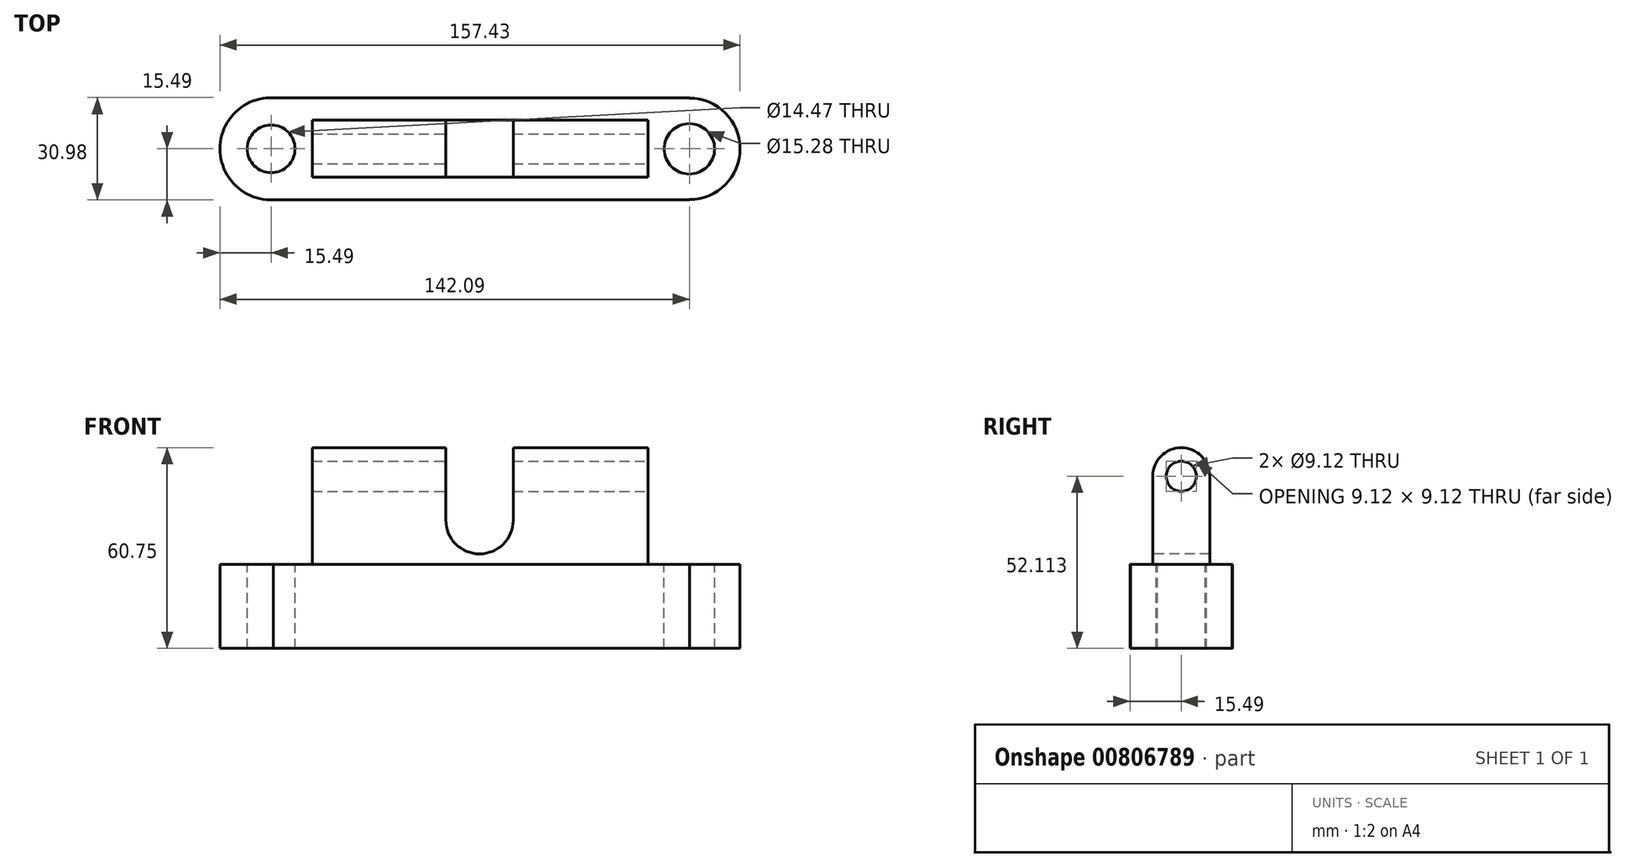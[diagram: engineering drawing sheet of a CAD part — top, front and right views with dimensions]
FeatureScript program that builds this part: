
annotation { "Feature Type Name" : "Feature", "Feature Type Description" : "" }
export const myFeature = defineFeature(function(context is Context, id is Id, definition is map)
    precondition{}
    {
        {
            var Q0;
            Q0=qCreatedBy(makeId("Top.planeOp"),FACE);
            var sketch = newSketch(context, id + "F0", { "sketchPlane" : qUnion([Q0])});
            skLineSegment(sketch, "E0.bottom", {"start": v(-63.3, 15.47) * mm, "end": v(-63.18, 15.47) * mm});
            skLineSegment(sketch, "E0.top", {"start": v(-63.3, -15.47) * mm, "end": v(63.3, -15.47) * mm});
            skLineSegment(sketch, "E0.left", {"start": v(-63.3, 15.47) * mm, "end": v(-63.3, -15.47) * mm});
            skLineSegment(sketch, "E0.right", {"start": v(63.3, 15.47) * mm, "end": v(63.3, -15.47) * mm});
            skPoint(sketch, "E0.middle", {"position": v(0, 0) * mm});
            skLineSegment(sketch, "E1", {"start": v(-63.18, 15.47) * mm, "end": v(63.3, 15.47) * mm});
            skArc(sketch, "E2", {"start": v(-62.58, 15.47) * mm, "mid": v(-78.79, 0) * mm, "end": v(-62.58, -15.47) * mm});
            skLineSegment(sketch, "E3", {"start": v(63.3, 15.47) * mm, "end": v(63.3, 15.47) * mm});
            skArc(sketch, "E4", {"start": v(63.69, -15.33) * mm, "mid": v(78.64, 0.2) * mm, "end": v(63.3, 15.34) * mm});
            skArc(sketch, "E5", {"start": v(63.3, -15.34) * mm, "mid": v(63.5, -15.34) * mm, "end": v(63.69, -15.33) * mm});
            skSolve(sketch);
        }
        {
            var Q0;
            Q0 = qSketchRegion(id + "F0", true);
            extrude(context, id + "F1", {"entities" : qUnion([Q0]), "depth" : 25.4 * mm, "offsetDistance" : 25.4 * mm});
        }
        {
            var Q0;
            Q0=qCreatedBy(makeId("Right.planeOp"),FACE);
            var sketch = newSketch(context, id + "F2", { "sketchPlane" : qUnion([Q0])});
            skLineSegment(sketch, "E6.bottom", {"start": v(8.64, 25.49) * mm, "end": v(-8.64, 25.49) * mm});
            skLineSegment(sketch, "E6.left", {"start": v(8.64, 25.49) * mm, "end": v(8.64, 52.11) * mm});
            skLineSegment(sketch, "E6.right", {"start": v(-8.64, 25.49) * mm, "end": v(-8.64, 52.11) * mm});
            skPoint(sketch, "E6.middle", {"position": v(0, 38.8) * mm});
            skArc(sketch, "E7", {"start": v(8.64, 52.11) * mm, "mid": v(0, 60.75) * mm, "end": v(-8.64, 52.11) * mm});
            skSolve(sketch);
        }
        {
            var Q0;
            Q0 = qSketchRegion(id + "F2", true);
            extrude(context, id + "F3", {"entities" : qUnion([Q0]), "endBound" : BoundingType.SYMMETRIC, "depth" : 101.6 * mm, "offsetDistance" : 25.4 * mm});
        }
        {
            var Q0;
            Q0=makeQuery(id+"F3.opExtrude","CAP_FACE",FACE,{"disambiguationData":[OSD([sQuery(id+"F2.wireOp",EDGE,"E6.bottom"),sQuery(id+"F2.wireOp",EDGE,"E6.left"),sQuery(id+"F2.wireOp",EDGE,"E6.right"),sQuery(id+"F2.wireOp",EDGE,"E7")])],"isStart":false});
            var sketch = newSketch(context, id + "F4", { "sketchPlane" : qUnion([Q0])});
            skCircle(sketch, "E8", {"center": v(0, 52.11) * mm, "radius": 4.56 * mm});
            skSolve(sketch);
        }
        {
            var Q0;
            Q0=makeQuery(id+"F4.imprint","IMPRINT",FACE,{"disambiguationData":[TD([[makeQuery(id+"F4.imprint","IMPRINT",EDGE,{"derivedFrom":sQuery(id+"F4.wireOp",EDGE,"E8")}),1.0]])]});
            extrude(context, id + "F5", {"entities" : qUnion([Q0]), "operationType" : NewBodyOperationType.REMOVE, "endBound" : BoundingType.THROUGH_ALL, "oppositeDirection" : true, "depth" : 25.4 * mm, "offsetDistance" : 25.4 * mm});
        }
        {
            var Q0;
            Q0=makeQuery(id+"F1.opExtrude","CAP_FACE",FACE,{"disambiguationData":[OSD([sQuery(id+"F0.wireOp",EDGE,"E0.top"),sQuery(id+"F0.wireOp",EDGE,"E0.right"),sQuery(id+"F0.wireOp",EDGE,"E1"),sQuery(id+"F0.wireOp",EDGE,"E2"),sQuery(id+"F0.wireOp",EDGE,"E4"),sQuery(id+"F0.wireOp",EDGE,"E5")])],"isStart":false});
            var sketch = newSketch(context, id + "F6", { "sketchPlane" : qUnion([Q0])});
            skCircle(sketch, "E9", {"center": v(-63.3, 0) * mm, "radius": 7.23 * mm});
            skSolve(sketch);
        }
        {
            var Q0;
            Q0 = qSketchRegion(id + "F6", true);
            extrude(context, id + "F7", {"entities" : qUnion([Q0]), "operationType" : NewBodyOperationType.REMOVE, "endBound" : BoundingType.THROUGH_ALL, "oppositeDirection" : true, "depth" : 25.4 * mm, "offsetDistance" : 25.4 * mm});
        }
        {
            var Q0;
            Q0=makeQuery(id+"F1.opExtrude","CAP_FACE",FACE,{"disambiguationData":[OSD([sQuery(id+"F0.wireOp",EDGE,"E0.top"),sQuery(id+"F0.wireOp",EDGE,"E0.right"),sQuery(id+"F0.wireOp",EDGE,"E1"),sQuery(id+"F0.wireOp",EDGE,"E2"),sQuery(id+"F0.wireOp",EDGE,"E4"),sQuery(id+"F0.wireOp",EDGE,"E5")])],"isStart":false});
            var sketch = newSketch(context, id + "F8", { "sketchPlane" : qUnion([Q0])});
            skCircle(sketch, "E10", {"center": v(63.3, 0) * mm, "radius": 7.64 * mm});
            skSolve(sketch);
        }
        {
            var Q0;
            Q0 = qSketchRegion(id + "F8", true);
            extrude(context, id + "F9", {"entities" : qUnion([Q0]), "operationType" : NewBodyOperationType.REMOVE, "endBound" : BoundingType.THROUGH_ALL, "oppositeDirection" : true, "depth" : 25.4 * mm, "offsetDistance" : 25.4 * mm});
        }
        {
            var Q0;
            Q0=makeQuery(id+"F3.opExtrude","SWEPT_FACE",FACE,{"disambiguationData":[OSD([sQuery(id+"F2.wireOp",EDGE,"E6.right")])]});
            var sketch = newSketch(context, id + "F10", { "sketchPlane" : qUnion([Q0])});
            skLineSegment(sketch, "E11.bottom", {"start": v(-10.41, 60.9) * mm, "end": v(9.98, 60.9) * mm});
            skLineSegment(sketch, "E11.top", {"start": v(-10.41, 38.8) * mm, "end": v(9.98, 38.8) * mm});
            skLineSegment(sketch, "E11.left", {"start": v(-10.41, 60.9) * mm, "end": v(-10.41, 38.8) * mm});
            skLineSegment(sketch, "E11.right", {"start": v(9.98, 60.9) * mm, "end": v(9.98, 38.8) * mm});
            skLineSegment(sketch, "E12", {"start": v(9.98, 38.8) * mm, "end": v(9.98, 38.8) * mm});
            skArc(sketch, "E13", {"start": v(-10.41, 38.8) * mm, "mid": v(-0.22, 28.6) * mm, "end": v(9.98, 38.8) * mm});
            skSolve(sketch);
        }
        {
            var Q0;
            Q0 = qSketchRegion(id + "F10", true);
            extrude(context, id + "F11", {"entities" : qUnion([Q0]), "operationType" : NewBodyOperationType.REMOVE, "endBound" : BoundingType.THROUGH_ALL, "oppositeDirection" : true, "depth" : 25.4 * mm, "offsetDistance" : 25.4 * mm});
        }
    });
